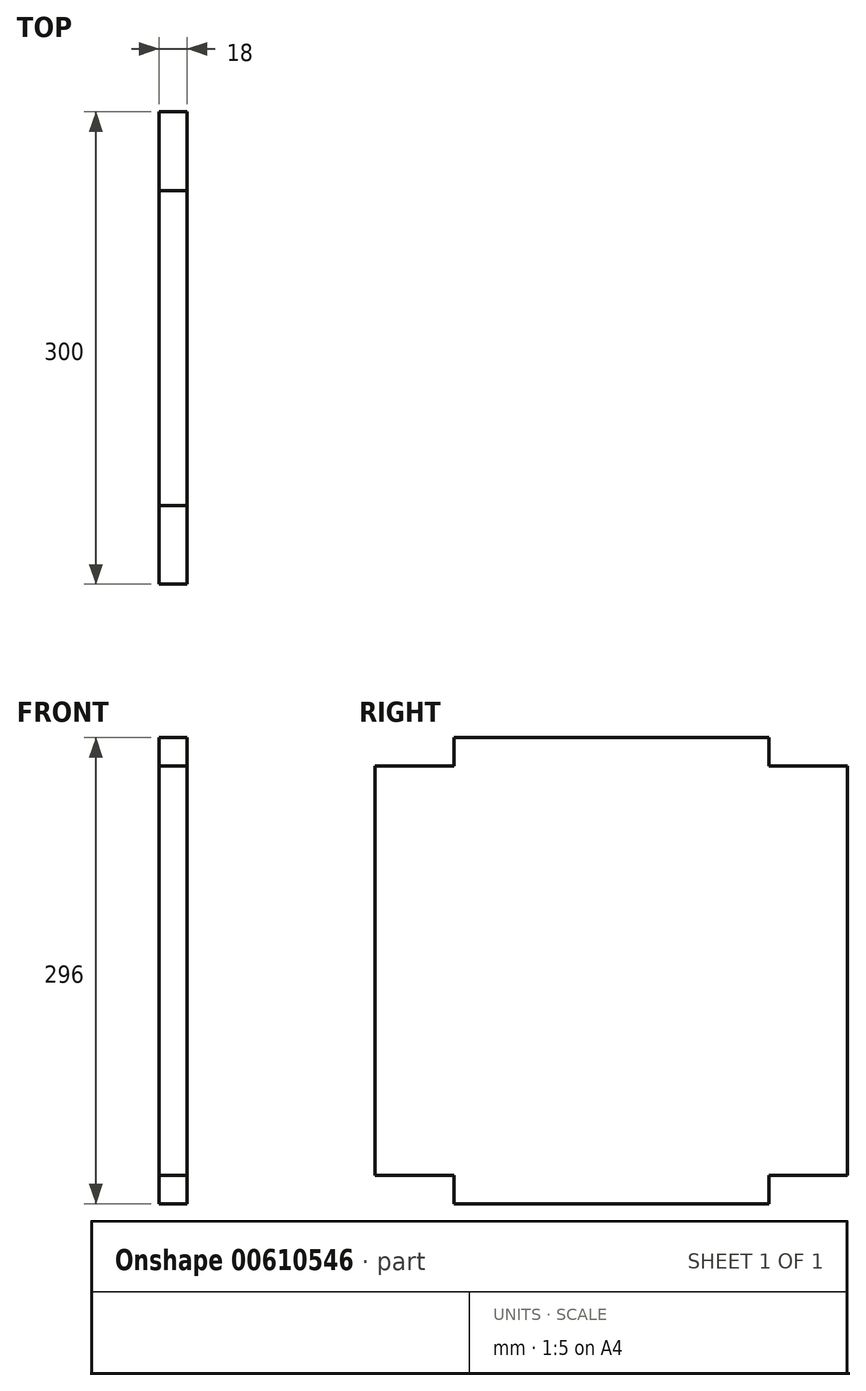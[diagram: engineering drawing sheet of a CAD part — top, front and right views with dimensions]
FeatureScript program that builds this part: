
annotation { "Feature Type Name" : "Feature", "Feature Type Description" : "" }
export const myFeature = defineFeature(function(context is Context, id is Id, definition is map)
    precondition{}
    {
        {
            var Q0;
            Q0=qCreatedBy(makeId("Right.planeOp"),FACE);
            var sketch = newSketch(context, id + "F0", { "sketchPlane" : qUnion([Q0])});
            skLineSegment(sketch, "E0.bottom", {"start": v(-85.18, -4.8) * mm, "end": v(-285.18, -4.8) * mm});
            skLineSegment(sketch, "E0.top", {"start": v(-85.18, 291.2) * mm, "end": v(-285.18, 291.2) * mm});
            skLineSegment(sketch, "E0.left", {"start": v(-35.18, 13.2) * mm, "end": v(-35.18, 273.2) * mm});
            skLineSegment(sketch, "E0.right", {"start": v(-335.18, 13.2) * mm, "end": v(-335.18, 273.2) * mm});
            skLineSegment(sketch, "E1.top", {"start": v(-35.18, 273.2) * mm, "end": v(-85.18, 273.2) * mm});
            skLineSegment(sketch, "E1.right", {"start": v(-85.18, 291.2) * mm, "end": v(-85.18, 273.2) * mm});
            skLineSegment(sketch, "E2.top", {"start": v(-285.18, 273.2) * mm, "end": v(-335.18, 273.2) * mm});
            skLineSegment(sketch, "E2.left", {"start": v(-285.18, 291.2) * mm, "end": v(-285.18, 273.2) * mm});
            skLineSegment(sketch, "E3.bottom", {"start": v(-285.18, 13.2) * mm, "end": v(-335.18, 13.2) * mm});
            skLineSegment(sketch, "E3.left", {"start": v(-285.18, 13.2) * mm, "end": v(-285.18, -4.8) * mm});
            skLineSegment(sketch, "E4.bottom", {"start": v(-35.18, 13.2) * mm, "end": v(-85.18, 13.2) * mm});
            skLineSegment(sketch, "E4.right", {"start": v(-85.18, 13.2) * mm, "end": v(-85.18, -4.8) * mm});
            skSolve(sketch);
        }
        {
            var Q0;
            Q0=makeQuery(id+"F0.imprint","IMPRINT",FACE,{"disambiguationData":[TD([[makeQuery(id+"F0.imprint","IMPRINT",EDGE,{"derivedFrom":sQuery(id+"F0.wireOp",EDGE,"E0.bottom")}),-1.0]])]});
            extrude(context, id + "F1", {"entities" : qUnion([Q0]), "depth" : 18 * mm, "offsetDistance" : 25 * mm});
        }
    });
